FCSTD DOCUMENT  (FreeCAD 0.18R16117 (Git))
Label: geometry
License: All rights reserved
LicenseURL: http://en.wikipedia.org/wiki/All_rights_reserved
objects: Part::Part2DObjectPython×6, App::DocumentObjectGroup×3
note: 6 computed .brp shape members not serialized (recipe doc carries the construction recipe); baked Part::Feature solids carry a one-line shape summary decoded from their .brp

FEATURE [Part::Part2DObjectPython] Rectangle001  # Draft 2D object (typed FeaturePython)
  ChamferSize = 0
  Columns = 1
  FilletRadius = 0
  Height = 34.0394
  Length = 31.2989
  MakeFace = true
  Placement = pos=(-32.0369,1.05601,0) rot=(0,0,1;0.504799rad)
  Rows = 1
FEATURE [Part::Part2DObjectPython] Wire001  # Draft 2D object (typed FeaturePython)
  ChamferSize = 0
  Closed = true
  End = (22.0135,28.0758,0)
  FilletRadius = 0
  Length = 123.255
  MakeFace = true
  Placement = pos=(30.8356,34.9613,0) rot=(0,0,1;0rad)
  Points = (5) [(0,0,0),(-18.7201,13.3407,0),(-26.4663,5.16415,0),(-1.29103,-35.7188,0),(-8.8221,-6.88555,0)]
  Start = (30.8356,34.9613,0)
  Subdivisions = 0
FEATURE [App::DocumentObjectGroup] Grupo  label="Terreo"
  Group = -> [Wire001,Rectangle001]
FEATURE [Part::Part2DObjectPython] Rectangle002  # Draft 2D object (typed FeaturePython)
  ChamferSize = 0
  Columns = 1
  FilletRadius = 0
  Height = 34.0394
  Length = 31.2989
  MakeFace = true
  Placement = pos=(-32.0369,1.05601,0) rot=(0,0,1;0.504799rad)
  Rows = 1
FEATURE [Part::Part2DObjectPython] Wire002  # Draft 2D object (typed FeaturePython)
  ChamferSize = 0
  Closed = true
  End = (22.0135,28.0758,0)
  FilletRadius = 0
  Length = 123.255
  MakeFace = true
  Placement = pos=(30.8356,34.9613,0) rot=(0,0,1;0rad)
  Points = (5) [(0,0,0),(-18.7201,13.3407,0),(-26.4663,5.16415,0),(-1.29103,-35.7188,0),(-8.8221,-6.88555,0)]
  Start = (30.8356,34.9613,0)
  Subdivisions = 0
FEATURE [App::DocumentObjectGroup] Grupo001  label="Tipo"
  Group = -> [Rectangle002,Wire002]
FEATURE [Part::Part2DObjectPython] Rectangle003  # Draft 2D object (typed FeaturePython)
  ChamferSize = 0
  Columns = 1
  FilletRadius = 0
  Height = 34.0394
  Length = 31.2989
  MakeFace = true
  Placement = pos=(-32.0369,1.05601,0) rot=(0,0,1;0.504799rad)
  Rows = 1
FEATURE [Part::Part2DObjectPython] Wire003  # Draft 2D object (typed FeaturePython)
  ChamferSize = 0
  Closed = true
  End = (22.0135,28.0758,0)
  FilletRadius = 0
  Length = 123.255
  MakeFace = true
  Placement = pos=(30.8356,34.9613,0) rot=(0,0,1;0rad)
  Points = (5) [(0,0,0),(-18.7201,13.3407,0),(-26.4663,5.16415,0),(-1.29103,-35.7188,0),(-8.8221,-6.88555,0)]
  Start = (30.8356,34.9613,0)
  Subdivisions = 0
FEATURE [App::DocumentObjectGroup] Grupo002  label="Cobertura"
  Group = -> [Rectangle003,Wire003]
